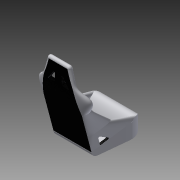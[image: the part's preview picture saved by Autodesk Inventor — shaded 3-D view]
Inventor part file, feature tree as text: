
AUTODESK INVENTOR PART (.ipt)
format: ipt  version: 2015 (Build 190159000, 159)  size: 1,276,416 bytes
history: native  units: in
note: dims shown in document units (in); Inventor stores cm internally (conversion verified against a paired STEP export)
features: other x2, imported_body x2, revolve x1
ambient origin geometry x8: Origin, YZ Plane, XZ Plane, XY Plane, X Axis, Y Axis, Z Axis, Center Point
bodies: Body1 (feature_tree), Body2 (feature_tree)
feature tree (5):
  revolve  "Revolve7"  [1 undecoded]
  other  "siege1"
  other  "Cut-Extrude11"
  imported_body  "Base1"
  imported_body  "Base2"
note: 1 required parameter value undecoded (feature->parameter linkage not recoverable at this tier; creation-order binding heuristic only, values carry confidence <= 0.55)
